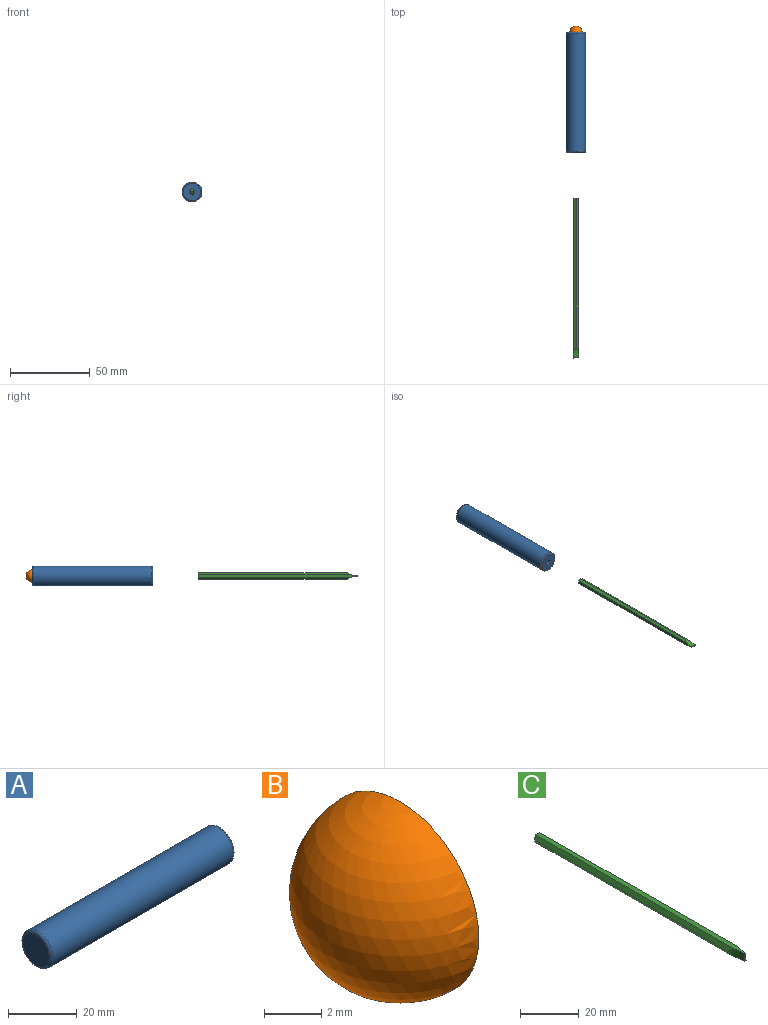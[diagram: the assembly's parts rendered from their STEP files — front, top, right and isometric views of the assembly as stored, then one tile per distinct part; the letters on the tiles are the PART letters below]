
ASSEMBLY  parts=3 mates=2
PART A: 12 faces, bbox 75.7x13.5x13.5 mm
  f0: plane 11x11mm, normal (1,0,0), area 85.7mm2, adj f3,f4,f5,f6,f7,f8,f11
  f1: cylinder r=6.25mm len=74.19mm, axis (-1,0,0), area 2913.4mm2, adj f10,f11
  f2: plane 11x11mm, normal (-1,0,0), area 95mm2, adj f10
  f3: plane 45.7x1.63mm, normal (0,0.86,0.5), area 86.4mm2, adj f0,f4,f8,f9
  f4: plane 45.7x1.89mm, normal (0,0,1), area 86.4mm2, adj f0,f3,f5,f9
  f5: plane 45.7x1.64mm, normal (0,-0.87,0.5), area 86.4mm2, adj f0,f4,f6,f9
  f6: plane 45.7x1.63mm, normal (0,-0.86,-0.5), area 86.4mm2, adj f0,f5,f7,f9
  f7: plane 45.7x1.89mm, normal (0,0,-1), area 86.4mm2, adj f0,f6,f8,f9
  f8: plane 45.7x1.64mm, normal (0,0.87,-0.5), area 86.4mm2, adj f0,f3,f7,f9
  f9: plane 3.78x3.28mm, normal (1,0,0), area 9.3mm2, adj f3,f4,f5,f6,f7,f8
  f10: torus R=5.5mm, axis (1,0,0), area 44.2mm2, adj f1,f2
  f11: torus R=5.5mm, axis (1,0,0), area 44.2mm2, adj f0,f1
PART B: 2 faces, bbox 3.9x7.8x7.8 mm
  f0: sphere r=3.9mm, area 95.3mm2, adj f1
  f1: plane 7.79x7.79mm, normal (1,0,0), area 47.7mm2, adj f0
PART C: 10 faces, bbox 3.8x100.3x3.3 mm
  f0: plane 95.37x1.64mm, normal (-0.87,0,-0.5), area 178.3mm2, adj f1,f3,f7,f8
  f1: plane 100.25x2.02mm, normal (0,0,-1), area 184.6mm2, adj f0,f4,f5,f7,f8,f9
  f2: plane 100.25x2.02mm, normal (0,0,1), area 184.6mm2, adj f3,f4,f6,f7,f8,f9
  f3: plane 95.37x1.64mm, normal (-0.87,0,0.5), area 178.3mm2, adj f0,f2,f7,f8
  f4: plane 3.27x0.54mm, normal (0,-1,0), area 1.8mm2, adj f1,f2,f8,f9
  f5: plane 95.37x1.64mm, normal (0.87,0,-0.5), area 178.3mm2, adj f1,f6,f7,f9
  f6: plane 95.37x1.64mm, normal (0.87,0,0.5), area 178.3mm2, adj f2,f5,f7,f9
  f7: plane 3.78x3.28mm, normal (0,1,0), area 9.3mm2, adj f0,f1,f2,f3,f5,f6
  f8: extruded ~6.77x3.28mm, area 19.9mm2, adj f0,f1,f2,f3,f4
  f9: extruded ~6.77x3.28mm, area 19.9mm2, adj f1,f2,f4,f5,f6
PLACE A rot(axis=(-0.58,0.58,-0.58),120deg) t=(-10.94,36.72,0.18)mm fixed
PLACE B rot(axis=(0,0,-1),90deg) t=(1.02,36.72,-11.78)mm
PLACE C rot(axis=(0,1,0),90deg) t=(1.02,-78.93,0.18)mm
MATE fastened B.f1 <-> A.f1  axis (0,-1,0) through (1.02,25.53,0.18)mm
MATE slider C.f7 <-> A.f1  axis (0,1,0) through (1.02,-78.93,0.18)mm
